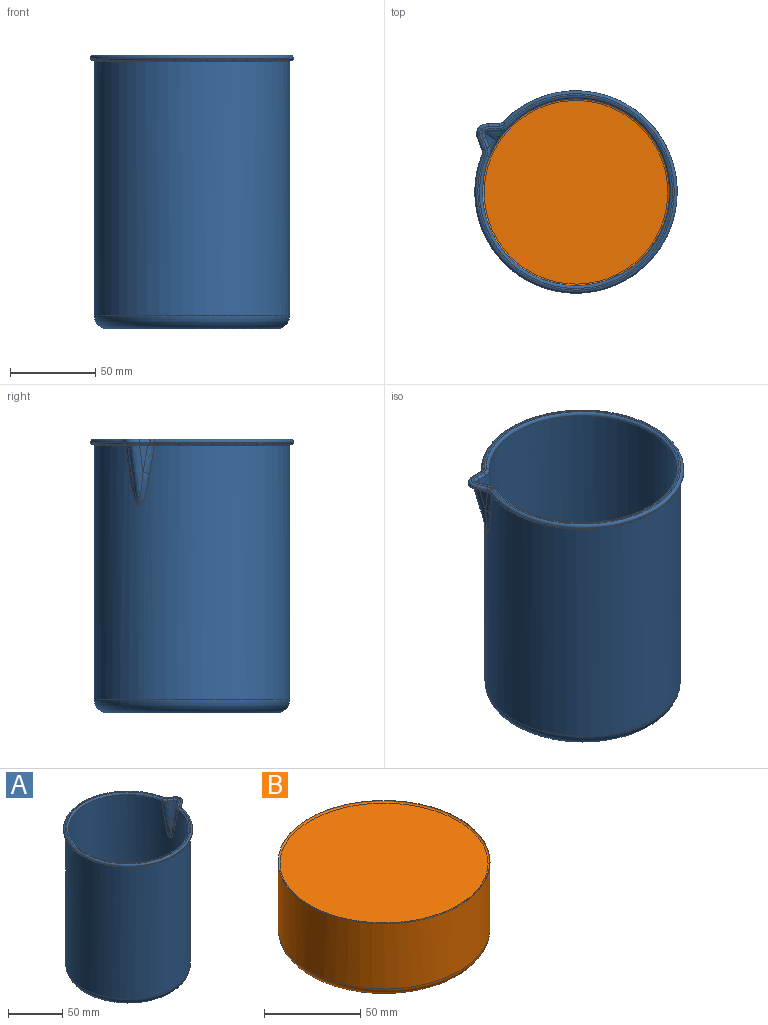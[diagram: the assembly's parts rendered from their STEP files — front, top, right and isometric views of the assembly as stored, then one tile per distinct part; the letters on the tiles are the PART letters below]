
ASSEMBLY  parts=2 mates=1
PART A: 50 faces, bbox 139.2x133.8x168.3 mm
  f0: plane 124.65x115.5mm, normal (0,0,1), area 376mm2, adj f26,f27,f28,f29,f30,f31,f32,f33
  f1: cylinder r=55mm len=151.25mm, axis (0,0,-1), area 51762.9mm2, adj f5,f6,f8,f9,f32
  f2: plane 99x99mm, normal (0,0,1), area 7697.7mm2, adj f5
  f3: plane 17.74x4.77mm, normal (-0.57,-0.81,0.14), area 52mm2, adj f7,f9,f36
  f4: plane 17.74x4.77mm, normal (-0.57,0.81,0.14), area 52mm2, adj f6,f7,f35
  f5: torus R=49.5mm, axis (0,0,1), area 2877.1mm2, adj f1,f2
  f6: offset ~26.95x12.16mm, area 111.6mm2, adj f1,f4,f8,f33
  f7: offset ~40.84x16mm, area 143.3mm2, adj f3,f4,f8,f37
  f8: offset ~24.29x19.87mm, area 175.4mm2, adj f1,f6,f7,f9
  f9: offset ~26.95x12.16mm, area 111.6mm2, adj f1,f3,f8,f34
  f10: plane 5.32x3.77mm, normal (0.58,-0.82,0), area 1.6mm2, adj f11,f15,f29,f40
  f11: extruded ~11.35x3.7mm, area 3.5mm2, adj f10,f12,f27,f38
  f12: plane 5.32x3.77mm, normal (0.58,0.82,0), area 1.6mm2, adj f11,f13,f26,f39
  f13: cylinder r=3mm len=1.88mm, axis (0,0,1), area 0.6mm2, adj f12,f14,f28,f41
  f14: cylinder r=59.5mm len=119mm, axis (0,0,1), area 87.8mm2, adj f13,f15,f30,f44
  f15: cylinder r=3mm len=1.88mm, axis (0,0,1), area 0.6mm2, adj f10,f14,f31,f42
  f16: plane 23.07x11.03mm, normal (0,0,-1), area 17.2mm2, adj f38,f39,f40,f41,f42,f43,f45,f46
  f17: plane 99x99mm, normal (0,0,-1), area 7697.7mm2, adj f18
  f18: torus R=49.5mm, axis (0,0,1), area 4310.5mm2, adj f17,f25
  f19: bspline ~19.29x14.88mm, area 120.2mm2, adj f20,f21,f23,f25
  f20: bspline ~16.96x6.24mm, area 66mm2, adj f19,f22,f25,f48
  f21: bspline ~40.7x14.81mm, area 268.7mm2, adj f19,f22,f24,f47
  f22: plane 15.77x4.26mm, normal (0.57,-0.81,-0.14), area 40.8mm2, adj f20,f21,f49
  f23: bspline ~16.96x6.24mm, area 66mm2, adj f19,f24,f25,f43
  f24: plane 15.77x4.26mm, normal (0.57,0.81,-0.14), area 40.8mm2, adj f21,f23,f45
  f25: cylinder r=57.5mm len=149mm, axis (0,0,-1), area 53350.8mm2, adj f18,f19,f20,f23,f46
  f26: cylinder r=1.75mm len=6.34mm, axis (-0.82,0.58,0), area 17.9mm2, adj f0,f12,f27,f28
  f27: bspline ~17.21x8.86mm, area 35.4mm2, adj f0,f11,f26,f29
  f28: torus R=4.75mm, axis (0,0,1), area 7.6mm2, adj f0,f13,f26,f30
  f29: cylinder r=1.75mm len=6.34mm, axis (0.82,0.58,0), area 17.9mm2, adj f0,f10,f27,f31
  f30: torus R=57.75mm, axis (0,0,1), area 954.7mm2, adj f0,f14,f28,f31
  f31: torus R=4.75mm, axis (0,0,1), area 7.6mm2, adj f0,f15,f29,f30
  f32: torus R=56.75mm, axis (0,0,1), area 903.7mm2, adj f0,f1,f33,f34
  f33: bspline ~5.4x4.27mm, area 14.1mm2, adj f0,f6,f32,f35
  f34: bspline ~5.4x4.27mm, area 14.1mm2, adj f0,f9,f32,f36
  f35: cylinder r=1.75mm len=5.77mm, axis (0.82,0.58,0), area 14.7mm2, adj f0,f4,f33,f37
  f36: cylinder r=1.75mm len=5.77mm, axis (-0.82,0.58,0), area 14.7mm2, adj f0,f3,f34,f37
  f37: bspline ~7.29x3.84mm, area 16.8mm2, adj f0,f7,f35,f36
  f38: bspline ~11.35x4.28mm, area 21.8mm2, adj f11,f16,f39,f40
  f39: bspline ~5.9x4.59mm, area 10.6mm2, adj f12,f16,f38,f41
  f40: bspline ~5.9x4.59mm, area 10.6mm2, adj f10,f16,f38,f42
  f41: bspline ~2.69x2.19mm, area 4.1mm2, adj f13,f16,f39,f44
  f42: bspline ~2.69x2.19mm, area 4.1mm2, adj f15,f16,f40,f44
  f43: bspline ~3.43x2.65mm, area 5.7mm2, adj f16,f23,f45,f46
  f44: bspline ~118.82x117.8mm, area 566.6mm2, adj f14,f41,f42,f46
  f45: bspline ~4.79x3.8mm, area 7.6mm2, adj f16,f24,f43,f47
  f46: bspline ~116.79x115.95mm, area 556.1mm2, adj f16,f25,f43,f44,f48
  f47: bspline ~9.7x3.85mm, area 15.6mm2, adj f16,f21,f45,f49
  f48: bspline ~3.43x2.65mm, area 5.7mm2, adj f16,f20,f46,f49
  f49: bspline ~4.79x3.8mm, area 7.6mm2, adj f16,f22,f47,f48
PART B: 5 faces, bbox 119x119x47.5 mm
  f0: plane 99x99mm, normal (0,0,-1), area 7697.7mm2, adj f1
  f1: torus R=49.5mm, axis (0,0,1), area 2849.2mm2, adj f0,f2
  f2: cylinder r=54.95mm len=109.9mm, axis (0,0,1), area 14499.2mm2, adj f1,f4
  f3: plane 107.94x107.94mm, normal (0,0,1), area 9146mm2, adj f4
  f4: bspline ~109.9x109.9mm, area 551.4mm2, adj f2,f3
PLACE A rot(axis=(0,0,1),147deg) t=(0,0,35)mm
PLACE B rot(axis=(0,0,-1),123deg) t=(0,0,35)mm
MATE fastened A.f1 <-> B.f1  axis (0,0,1) through (0,0,35)mm
